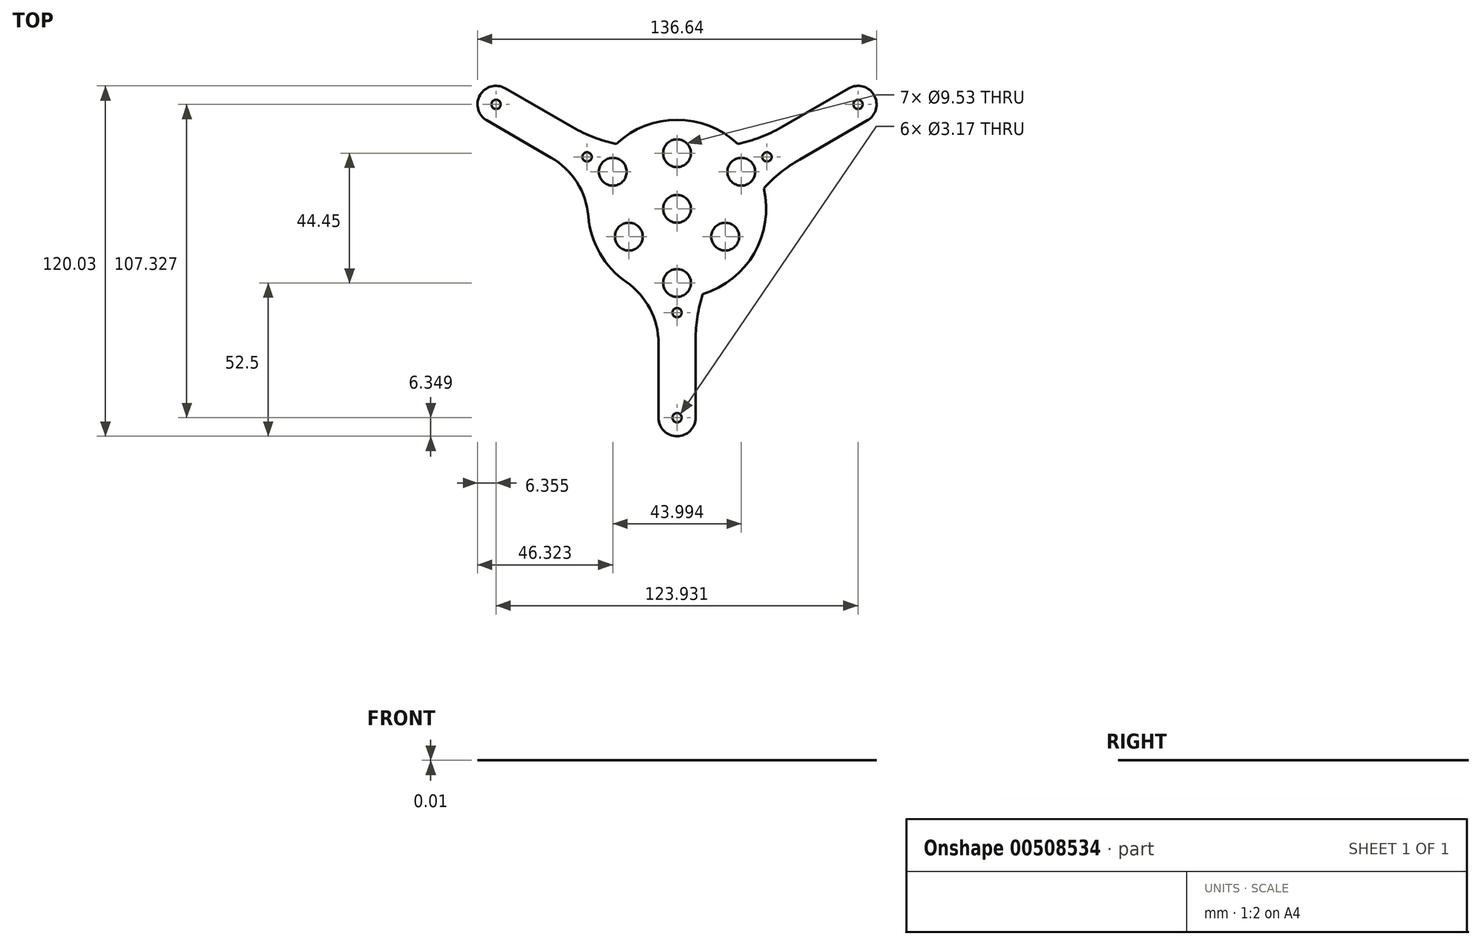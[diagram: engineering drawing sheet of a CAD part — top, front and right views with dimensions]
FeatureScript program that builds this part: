
annotation { "Feature Type Name" : "Feature", "Feature Type Description" : "" }
export const myFeature = defineFeature(function(context is Context, id is Id, definition is map)
    precondition{}
    {
        {
            var Q0;
            Q0=qCreatedBy(makeId("Top.planeOp"),FACE);
            var sketch = newSketch(context, id + "F0", { "sketchPlane" : qUnion([Q0])});
            skCircle(sketch, "E0.cCircle", {"center": v(0, 0) * mm, "radius": 44.45 * mm, "construction": true});
            skLineSegment(sketch, "E0.0", {"start": v(38.5, 22.23) * mm, "end": v(0, -44.45) * mm});
            skLineSegment(sketch, "E0.1", {"start": v(0, -44.45) * mm, "end": v(-38.5, 22.22) * mm});
            skLineSegment(sketch, "E0.2", {"start": v(-38.5, 22.22) * mm, "end": v(38.5, 22.22) * mm});
            skCircle(sketch, "E1.cCircle", {"center": v(0, 0) * mm, "radius": 25.4 * mm, "construction": true});
            skLineSegment(sketch, "E1.0", {"start": v(22, 12.7) * mm, "end": v(0, -25.4) * mm, "construction": true});
            skLineSegment(sketch, "E1.1", {"start": v(0, -25.4) * mm, "end": v(-22, 12.7) * mm, "construction": true});
            skLineSegment(sketch, "E1.2", {"start": v(-22, 12.7) * mm, "end": v(22, 12.7) * mm, "construction": true});
            skCircle(sketch, "E2.cCircle", {"center": v(0, 0) * mm, "radius": 35.56 * mm, "construction": true});
            skLineSegment(sketch, "E2.0", {"start": v(30.8, 17.78) * mm, "end": v(0, -35.56) * mm, "construction": true});
            skLineSegment(sketch, "E2.1", {"start": v(0, -35.56) * mm, "end": v(-30.8, 17.78) * mm, "construction": true});
            skLineSegment(sketch, "E2.2", {"start": v(-30.8, 17.78) * mm, "end": v(30.8, 17.78) * mm, "construction": true});
            skCircle(sketch, "E3", {"center": v(-22, 12.7) * mm, "radius": 4.76 * mm});
            skCircle(sketch, "E4", {"center": v(22, 12.7) * mm, "radius": 4.76 * mm});
            skCircle(sketch, "E5", {"center": v(0, -25.4) * mm, "radius": 4.76 * mm});
            skCircle(sketch, "E6", {"center": v(-30.8, 17.78) * mm, "radius": 1.59 * mm});
            skCircle(sketch, "E7", {"center": v(30.8, 17.78) * mm, "radius": 1.59 * mm});
            skCircle(sketch, "E8", {"center": v(0, -35.56) * mm, "radius": 1.59 * mm});
            skLineSegment(sketch, "E9", {"start": v(-6.35, -33.45) * mm, "end": v(-6.35, -71.55) * mm});
            skLineSegment(sketch, "E10", {"start": v(6.35, -33.45) * mm, "end": v(6.35, -71.55) * mm});
            skArc(sketch, "E11", {"start": v(-6.35, -71.55) * mm, "mid": v(0, -77.9) * mm, "end": v(6.35, -71.55) * mm});
            skArc(sketch, "E12.1.0", {"start": v(65.14, 30.28) * mm, "mid": v(67.46, 38.95) * mm, "end": v(58.8, 41.28) * mm});
            skLineSegment(sketch, "E12.1.1", {"start": v(25.8, 22.22) * mm, "end": v(58.8, 41.28) * mm});
            skLineSegment(sketch, "E12.1.2", {"start": v(32.14, 11.23) * mm, "end": v(65.14, 30.28) * mm});
            skArc(sketch, "E12.2.0", {"start": v(-58.8, 41.28) * mm, "mid": v(-67.46, 38.95) * mm, "end": v(-65.14, 30.28) * mm});
            skLineSegment(sketch, "E12.2.1", {"start": v(-32.14, 11.23) * mm, "end": v(-65.14, 30.28) * mm});
            skLineSegment(sketch, "E12.2.2", {"start": v(-25.8, 22.22) * mm, "end": v(-58.8, 41.27) * mm});
            skCircle(sketch, "E13", {"center": v(-61.97, 35.78) * mm, "radius": 1.59 * mm});
            skCircle(sketch, "E14", {"center": v(61.97, 35.78) * mm, "radius": 1.59 * mm});
            skCircle(sketch, "E15", {"center": v(0, -71.55) * mm, "radius": 1.59 * mm});
            skCircle(sketch, "E16", {"center": v(0, 0) * mm, "radius": 4.76 * mm});
            skCircle(sketch, "E17.cCircle", {"center": v(0, 0) * mm, "radius": 38.1 * mm, "construction": true});
            skLineSegment(sketch, "E17.0", {"start": v(-33, 19.05) * mm, "end": v(33, 19.05) * mm, "construction": true});
            skLineSegment(sketch, "E17.1", {"start": v(33, 19.05) * mm, "end": v(0, -38.1) * mm, "construction": true});
            skLineSegment(sketch, "E17.2", {"start": v(0, -38.1) * mm, "end": v(-33, 19.05) * mm, "construction": true});
            skCircle(sketch, "E18", {"center": v(16.5, -9.53) * mm, "radius": 4.76 * mm});
            skCircle(sketch, "E19", {"center": v(-16.5, -9.53) * mm, "radius": 4.76 * mm});
            skCircle(sketch, "E20", {"center": v(0, 19.05) * mm, "radius": 4.76 * mm});
            skCircle(sketch, "E21", {"center": v(0, 0) * mm, "radius": 30.48 * mm});
            skSolve(sketch);
        }
        {
            var Q0;
            Q0 = qSketchRegion(id + "F0", true);
            extrude(context, id + "F1", {"entities" : qUnion([Q0]), "depth" : 1 / 101.6 * mm});
        }
        {
            var Q0;
            Q0=makeQuery(id+"F1.opExtrude","SWEPT_EDGE",EDGE,{"disambiguationData":[OSD([sQuery(id+"F0.wireOp",EDGE,"E0.0"),sQuery(id+"F0.wireOp",EDGE,"E12.1.2")])]});
            var Q1;
            Q1=makeQuery(id+"F1.opExtrude","SWEPT_EDGE",EDGE,{"disambiguationData":[OSD([sQuery(id+"F0.wireOp",EDGE,"E0.2"),sQuery(id+"F0.wireOp",EDGE,"E12.1.1")])]});
            var Q2;
            Q2=makeQuery(id+"F1.opExtrude","SWEPT_EDGE",EDGE,{"disambiguationData":[OSD([sQuery(id+"F0.wireOp",EDGE,"E0.2"),sQuery(id+"F0.wireOp",EDGE,"E12.2.2")])]});
            var Q3;
            Q3=makeQuery(id+"F1.opExtrude","SWEPT_EDGE",EDGE,{"disambiguationData":[OSD([sQuery(id+"F0.wireOp",EDGE,"E0.1"),sQuery(id+"F0.wireOp",EDGE,"E12.2.1")])]});
            var Q4;
            Q4=makeQuery(id+"F1.opExtrude","SWEPT_EDGE",EDGE,{"disambiguationData":[OSD([sQuery(id+"F0.wireOp",EDGE,"E0.1"),sQuery(id+"F0.wireOp",EDGE,"E9")])]});
            var Q5;
            Q5=makeQuery(id+"F1.opExtrude","SWEPT_EDGE",EDGE,{"disambiguationData":[OSD([sQuery(id+"F0.wireOp",EDGE,"E0.0"),sQuery(id+"F0.wireOp",EDGE,"E10")])]});
            fillet(context, id + "F2", {"entities" : qUnion([Q0, Q1, Q2, Q3, Q4, Q5]), "radius" : 50.8 * mm, "tangentPropagation" : true, "allowEdgeOverflow" : false});
        }
        {
            var Q0;
            {var subQ0=sQuery(id+"F0.wireOp",EDGE,"E21");var subQ1=sQuery(id+"F0.wireOp",EDGE,"E0.1");Q0=makeQuery(id+"F2.opFillet","BLEND_EDGE",EDGE,{"blendedFrom":[makeQuery(id+"F1.opExtrude","SWEPT_EDGE",EDGE,{"disambiguationData":[OSD([subQ1,sQuery(id+"F0.wireOp",EDGE,"E12.2.1")])]}),makeQuery(id+"F1.opExtrude","SWEPT_FACE",FACE,{"disambiguationData":[OSD([subQ0]),TDD([makeQuery(id+"F0.imprint","IMPRINT",EDGE,{"disambiguationData":[TD([[makeQuery(id+"F0.imprint","INTERSECT",VERTEX,{"disambiguationData":[OD(0.0)],"derivedFrom":[subQ1,subQ0]}),1.0]])],"derivedFrom":subQ0})])]})],"blendedInto":[makeQuery(id+"F1.opExtrude","SWEPT_FACE",FACE,{"disambiguationData":[OSD([subQ0]),TDD([makeQuery(id+"F0.imprint","IMPRINT",EDGE,{"disambiguationData":[TD([[makeQuery(id+"F0.imprint","INTERSECT",VERTEX,{"disambiguationData":[OD(0.0)],"derivedFrom":[subQ1,subQ0]}),1.0]])],"derivedFrom":subQ0})])]})]});}
            var Q1;
            {var subQ0=sQuery(id+"F0.wireOp",EDGE,"E21");var subQ1=sQuery(id+"F0.wireOp",EDGE,"E0.1");Q1=makeQuery(id+"F2.opFillet","BLEND_EDGE",EDGE,{"blendedFrom":[makeQuery(id+"F1.opExtrude","SWEPT_EDGE",EDGE,{"disambiguationData":[OSD([subQ1,sQuery(id+"F0.wireOp",EDGE,"E9")])]}),makeQuery(id+"F1.opExtrude","SWEPT_FACE",FACE,{"disambiguationData":[OSD([subQ0]),TDD([makeQuery(id+"F0.imprint","IMPRINT",EDGE,{"disambiguationData":[TD([[makeQuery(id+"F0.imprint","INTERSECT",VERTEX,{"disambiguationData":[OD(0.0)],"derivedFrom":[subQ1,subQ0]}),1.0]])],"derivedFrom":subQ0})])]})],"blendedInto":[makeQuery(id+"F1.opExtrude","SWEPT_FACE",FACE,{"disambiguationData":[OSD([subQ0]),TDD([makeQuery(id+"F0.imprint","IMPRINT",EDGE,{"disambiguationData":[TD([[makeQuery(id+"F0.imprint","INTERSECT",VERTEX,{"disambiguationData":[OD(0.0)],"derivedFrom":[subQ1,subQ0]}),1.0]])],"derivedFrom":subQ0})])]})]});}
            var Q2;
            {var subQ0=sQuery(id+"F0.wireOp",EDGE,"E21");var subQ1=sQuery(id+"F0.wireOp",EDGE,"E0.0");Q2=makeQuery(id+"F2.opFillet","BLEND_EDGE",EDGE,{"blendedFrom":[makeQuery(id+"F1.opExtrude","SWEPT_EDGE",EDGE,{"disambiguationData":[OSD([subQ1,sQuery(id+"F0.wireOp",EDGE,"E10")])]}),makeQuery(id+"F1.opExtrude","SWEPT_FACE",FACE,{"disambiguationData":[OSD([subQ0]),TDD([makeQuery(id+"F0.imprint","IMPRINT",EDGE,{"disambiguationData":[TD([[makeQuery(id+"F0.imprint","INTERSECT",VERTEX,{"disambiguationData":[OD(0.0)],"derivedFrom":[subQ1,subQ0]}),1.0]])],"derivedFrom":subQ0})])]})],"blendedInto":[makeQuery(id+"F1.opExtrude","SWEPT_FACE",FACE,{"disambiguationData":[OSD([subQ0]),TDD([makeQuery(id+"F0.imprint","IMPRINT",EDGE,{"disambiguationData":[TD([[makeQuery(id+"F0.imprint","INTERSECT",VERTEX,{"disambiguationData":[OD(0.0)],"derivedFrom":[subQ1,subQ0]}),1.0]])],"derivedFrom":subQ0})])]})]});}
            var Q3;
            {var subQ0=sQuery(id+"F0.wireOp",EDGE,"E21");var subQ1=sQuery(id+"F0.wireOp",EDGE,"E0.0");Q3=makeQuery(id+"F2.opFillet","BLEND_EDGE",EDGE,{"blendedFrom":[makeQuery(id+"F1.opExtrude","SWEPT_EDGE",EDGE,{"disambiguationData":[OSD([subQ1,sQuery(id+"F0.wireOp",EDGE,"E12.1.2")])]}),makeQuery(id+"F1.opExtrude","SWEPT_FACE",FACE,{"disambiguationData":[OSD([subQ0]),TDD([makeQuery(id+"F0.imprint","IMPRINT",EDGE,{"disambiguationData":[TD([[makeQuery(id+"F0.imprint","INTERSECT",VERTEX,{"disambiguationData":[OD(0.0)],"derivedFrom":[subQ1,subQ0]}),1.0]])],"derivedFrom":subQ0})])]})],"blendedInto":[makeQuery(id+"F1.opExtrude","SWEPT_FACE",FACE,{"disambiguationData":[OSD([subQ0]),TDD([makeQuery(id+"F0.imprint","IMPRINT",EDGE,{"disambiguationData":[TD([[makeQuery(id+"F0.imprint","INTERSECT",VERTEX,{"disambiguationData":[OD(0.0)],"derivedFrom":[subQ1,subQ0]}),1.0]])],"derivedFrom":subQ0})])]})]});}
            var Q4;
            {var subQ0=sQuery(id+"F0.wireOp",EDGE,"E21");var subQ1=sQuery(id+"F0.wireOp",EDGE,"E0.2");Q4=makeQuery(id+"F2.opFillet","BLEND_EDGE",EDGE,{"blendedFrom":[makeQuery(id+"F1.opExtrude","SWEPT_EDGE",EDGE,{"disambiguationData":[OSD([subQ1,sQuery(id+"F0.wireOp",EDGE,"E12.1.1")])]}),makeQuery(id+"F1.opExtrude","SWEPT_FACE",FACE,{"disambiguationData":[OSD([subQ0]),TDD([makeQuery(id+"F0.imprint","IMPRINT",EDGE,{"disambiguationData":[TD([[makeQuery(id+"F0.imprint","INTERSECT",VERTEX,{"disambiguationData":[OD(0.0)],"derivedFrom":[subQ1,subQ0]}),1.0]])],"derivedFrom":subQ0})])]})],"blendedInto":[makeQuery(id+"F1.opExtrude","SWEPT_FACE",FACE,{"disambiguationData":[OSD([subQ0]),TDD([makeQuery(id+"F0.imprint","IMPRINT",EDGE,{"disambiguationData":[TD([[makeQuery(id+"F0.imprint","INTERSECT",VERTEX,{"disambiguationData":[OD(0.0)],"derivedFrom":[subQ1,subQ0]}),1.0]])],"derivedFrom":subQ0})])]})]});}
            var Q5;
            {var subQ0=sQuery(id+"F0.wireOp",EDGE,"E21");var subQ1=sQuery(id+"F0.wireOp",EDGE,"E0.2");Q5=makeQuery(id+"F2.opFillet","BLEND_EDGE",EDGE,{"blendedFrom":[makeQuery(id+"F1.opExtrude","SWEPT_EDGE",EDGE,{"disambiguationData":[OSD([subQ1,sQuery(id+"F0.wireOp",EDGE,"E12.2.2")])]}),makeQuery(id+"F1.opExtrude","SWEPT_FACE",FACE,{"disambiguationData":[OSD([subQ0]),TDD([makeQuery(id+"F0.imprint","IMPRINT",EDGE,{"disambiguationData":[TD([[makeQuery(id+"F0.imprint","INTERSECT",VERTEX,{"disambiguationData":[OD(0.0)],"derivedFrom":[subQ1,subQ0]}),1.0]])],"derivedFrom":subQ0})])]})],"blendedInto":[makeQuery(id+"F1.opExtrude","SWEPT_FACE",FACE,{"disambiguationData":[OSD([subQ0]),TDD([makeQuery(id+"F0.imprint","IMPRINT",EDGE,{"disambiguationData":[TD([[makeQuery(id+"F0.imprint","INTERSECT",VERTEX,{"disambiguationData":[OD(0.0)],"derivedFrom":[subQ1,subQ0]}),1.0]])],"derivedFrom":subQ0})])]})]});}
            fillet(context, id + "F3", {"entities" : qUnion([Q0, Q1, Q2, Q3, Q4, Q5]), "radius" : 25.66 * mm, "tangentPropagation" : true, "allowEdgeOverflow" : false});
        }
    });
